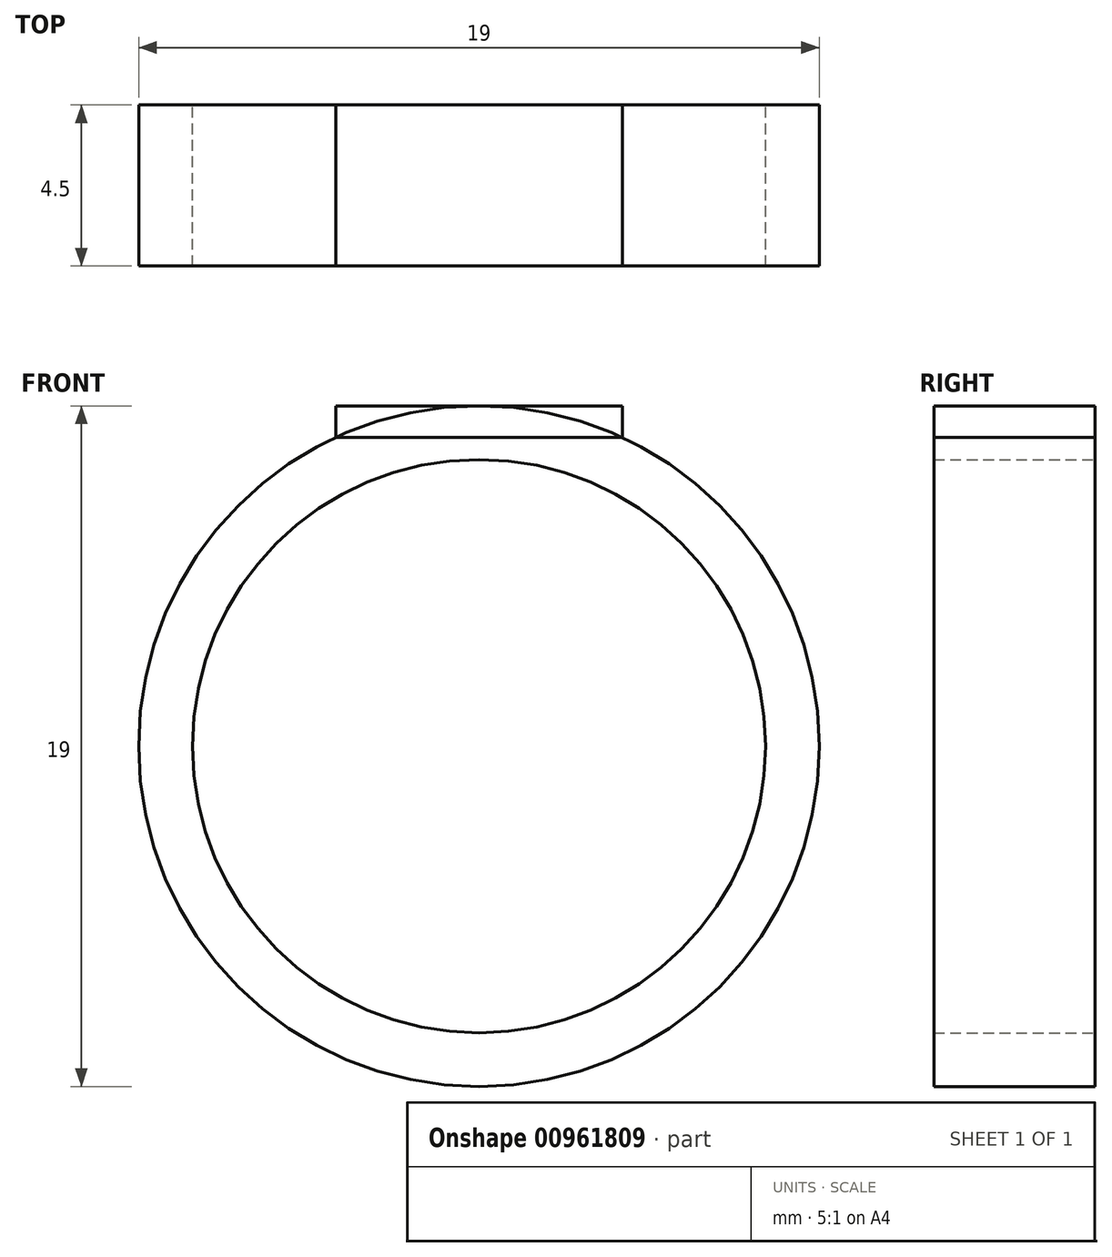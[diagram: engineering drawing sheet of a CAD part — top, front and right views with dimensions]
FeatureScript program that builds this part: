
annotation { "Feature Type Name" : "Feature", "Feature Type Description" : "" }
export const myFeature = defineFeature(function(context is Context, id is Id, definition is map)
    precondition{}
    {
        {
            var Q0;
            Q0=qCreatedBy(makeId("Front.planeOp"),FACE);
            var sketch = newSketch(context, id + "F0", { "sketchPlane" : qUnion([Q0])});
            skCircle(sketch, "E0", {"center": v(0, 0) * mm, "radius": 8 * mm});
            skCircle(sketch, "E1", {"center": v(0, 0) * mm, "radius": 9.5 * mm});
            skSolve(sketch);
        }
        {
            var Q0;
            Q0=makeQuery(id+"F0.imprint","IMPRINT",FACE,{"disambiguationData":[TD([[makeQuery(id+"F0.imprint","IMPRINT",EDGE,{"derivedFrom":sQuery(id+"F0.wireOp",EDGE,"E0")}),-1.0]])]});
            extrude(context, id + "F1", {"entities" : qUnion([Q0]), "depth" : 4.5 * mm, "offsetDistance" : 25 * mm});
        }
        {
            var Q0;
            Q0=qCreatedBy(makeId("Front.planeOp"),FACE);
            var sketch = newSketch(context, id + "F2", { "sketchPlane" : qUnion([Q0])});
            skLineSegment(sketch, "E2", {"start": v(-4, 9.5) * mm, "end": v(4, 9.5) * mm});
            skLineSegment(sketch, "E3", {"start": v(4, 9.5) * mm, "end": v(4, 8.62) * mm});
            skLineSegment(sketch, "E4", {"start": v(-4, 9.5) * mm, "end": v(-4, 8.62) * mm});
            skLineSegment(sketch, "E5", {"start": v(-4, 8.62) * mm, "end": v(4, 8.62) * mm});
            skSolve(sketch);
        }
        {
            var Q0;
            Q0=qSketchRegion(id+"F2",true);
            extrude(context, id + "F3", {"entities" : qUnion([Q0]), "depth" : 4.5 * mm, "offsetDistance" : 25 * mm});
        }
    });
